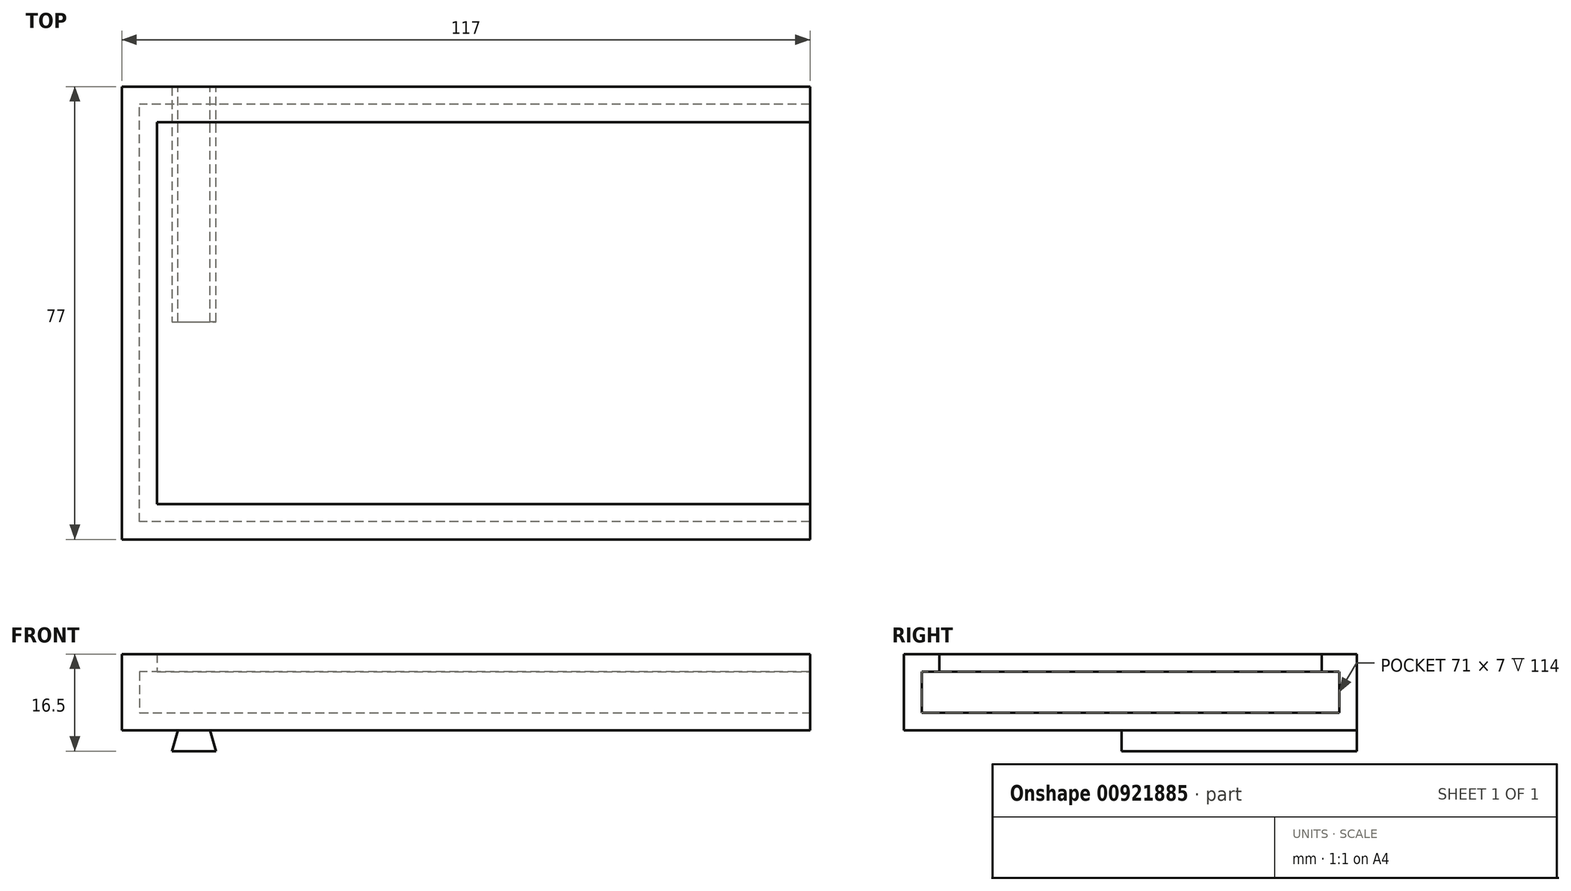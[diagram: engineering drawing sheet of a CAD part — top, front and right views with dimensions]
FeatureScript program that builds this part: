
annotation { "Feature Type Name" : "Feature", "Feature Type Description" : "" }
export const myFeature = defineFeature(function(context is Context, id is Id, definition is map)
    precondition{}
    {
        {
            var Q0;
            Q0=qCreatedBy(makeId("Top.planeOp"),FACE);
            var sketch = newSketch(context, id + "F0", { "sketchPlane" : qUnion([Q0])});
            skLineSegment(sketch, "E0.bottom", {"start": v(0, 0) * mm, "end": v(117, 0) * mm});
            skLineSegment(sketch, "E0.top", {"start": v(0, 77) * mm, "end": v(117, 77) * mm});
            skLineSegment(sketch, "E0.left", {"start": v(0, 0) * mm, "end": v(0, 77) * mm});
            skLineSegment(sketch, "E0.right", {"start": v(117, 0) * mm, "end": v(117, 77) * mm});
            skSolve(sketch);
        }
        {
            var Q0;
            Q0 = qSketchRegion(id + "F0", true);
            var Q1;
            Q1=makeQuery(id+"F0.imprint","IMPRINT",FACE,{"disambiguationData":[TD([[makeQuery(id+"F0.imprint","IMPRINT",EDGE,{"derivedFrom":sQuery(id+"F0.wireOp",EDGE,"E0.bottom")}),1.0]])]});
            extrude(context, id + "F1", {"entities" : qUnion([Q0, Q1]), "depth" : 3 * mm, "offsetDistance" : 25 * mm});
        }
        {
            var Q0;
            Q0=makeQuery(id+"F1.opExtrude","CAP_FACE",FACE,{"disambiguationData":[OSD([sQuery(id+"F0.wireOp",EDGE,"E0.bottom"),sQuery(id+"F0.wireOp",EDGE,"E0.top"),sQuery(id+"F0.wireOp",EDGE,"E0.left"),sQuery(id+"F0.wireOp",EDGE,"E0.right")])],"isStart":false});
            var sketch = newSketch(context, id + "F2", { "sketchPlane" : qUnion([Q0])});
            skLineSegment(sketch, "E1", {"start": v(117, 3) * mm, "end": v(3, 3) * mm});
            skLineSegment(sketch, "E2", {"start": v(3, 3) * mm, "end": v(3, 74) * mm});
            skLineSegment(sketch, "E3", {"start": v(3, 74) * mm, "end": v(117, 74) * mm});
            skSolve(sketch);
        }
        {
            var Q0;
            Q0 = qSketchRegion(id + "F2", true);
            var Q1;
            {var subQ2=sQuery(id+"F2.wireOp",EDGE,"E1");Q1=makeQuery(id+"F2.imprint","IMPRINT",FACE,{"disambiguationData":[TD([[makeQuery(id+"F2.imprint","IMPRINT",EDGE,{"derivedFrom":subQ2}),1.0]])]});}
            extrude(context, id + "F3", {"entities" : qUnion([Q0, Q1]), "operationType" : NewBodyOperationType.ADD, "depth" : 10 * mm, "offsetDistance" : 25 * mm});
        }
        {
            var Q0;
            Q0=makeQuery(id+"F3.opExtrude","SWEPT_FACE",FACE,{"disambiguationData":[OSD([sQuery(id+"F2.wireOp",EDGE,"E2")])]});
            var sketch = newSketch(context, id + "F4", { "sketchPlane" : qUnion([Q0])});
            skLineSegment(sketch, "E4", {"start": v(3, 10) * mm, "end": v(74, 10) * mm});
            skSolve(sketch);
        }
        {
            var Q0;
            Q0 = qSketchRegion(id + "F4", true);
            var Q1;
            {var subQ0=sQuery(id+"F4.wireOp",EDGE,"E4");Q1=makeQuery(id+"F4.imprint","IMPRINT",FACE,{"disambiguationData":[TD([[makeQuery(id+"F4.imprint","IMPRINT",EDGE,{"derivedFrom":subQ0}),1.0]])]});}
            extrude(context, id + "F5", {"entities" : qUnion([Q0, Q1]), "operationType" : NewBodyOperationType.ADD, "depth" : 3 * mm, "offsetDistance" : 25 * mm});
        }
        {
            var Q0;
            Q0=makeQuery(id+"F3.opExtrude","SWEPT_FACE",FACE,{"disambiguationData":[OSD([sQuery(id+"F2.wireOp",EDGE,"E1")])]});
            var sketch = newSketch(context, id + "F6", { "sketchPlane" : qUnion([Q0])});
            skLineSegment(sketch, "E5", {"start": v(-6, 10) * mm, "end": v(-117, 10) * mm});
            skSolve(sketch);
        }
        {
            var Q0;
            Q0 = qSketchRegion(id + "F6", true);
            var Q1;
            {var subQ0=sQuery(id+"F6.wireOp",EDGE,"E5");Q1=makeQuery(id+"F6.imprint","IMPRINT",FACE,{"disambiguationData":[TD([[makeQuery(id+"F6.imprint","IMPRINT",EDGE,{"derivedFrom":subQ0}),-1.0]])]});}
            extrude(context, id + "F7", {"entities" : qUnion([Q0, Q1]), "operationType" : NewBodyOperationType.ADD, "depth" : 3 * mm, "offsetDistance" : 25 * mm});
        }
        {
            var Q0;
            Q0=makeQuery(id+"F3.opExtrude","SWEPT_FACE",FACE,{"disambiguationData":[OSD([sQuery(id+"F2.wireOp",EDGE,"E3")])]});
            var sketch = newSketch(context, id + "F8", { "sketchPlane" : qUnion([Q0])});
            skLineSegment(sketch, "E6", {"start": v(6, 10) * mm, "end": v(117, 10) * mm});
            skSolve(sketch);
        }
        {
            var Q0;
            Q0 = qSketchRegion(id + "F8", true);
            var Q1;
            {var subQ0=sQuery(id+"F8.wireOp",EDGE,"E6");Q1=makeQuery(id+"F8.imprint","IMPRINT",FACE,{"disambiguationData":[TD([[makeQuery(id+"F8.imprint","IMPRINT",EDGE,{"derivedFrom":subQ0}),1.0]])]});}
            extrude(context, id + "F9", {"entities" : qUnion([Q0, Q1]), "operationType" : NewBodyOperationType.ADD, "depth" : 3 * mm, "offsetDistance" : 25 * mm});
        }
        {
            var Q0;
            Q0=makeQuery(id+"F1.opExtrude","CAP_FACE",FACE,{"disambiguationData":[OSD([sQuery(id+"F0.wireOp",EDGE,"E0.bottom"),sQuery(id+"F0.wireOp",EDGE,"E0.top"),sQuery(id+"F0.wireOp",EDGE,"E0.left"),sQuery(id+"F0.wireOp",EDGE,"E0.right")])],"isStart":true});
            var sketch = newSketch(context, id + "F10", { "sketchPlane" : qUnion([Q0])});
            skLineSegment(sketch, "E7", {"start": v(8.5, -77) * mm, "end": v(8.5, -37) * mm});
            skLineSegment(sketch, "E8", {"start": v(8.5, -37) * mm, "end": v(16, -37) * mm});
            skLineSegment(sketch, "E9", {"start": v(16, -37) * mm, "end": v(16, -77) * mm});
            skSolve(sketch);
        }
        {
            var Q0;
            Q0 = qSketchRegion(id + "F10", true);
            var Q1;
            {var subQ0=sQuery(id+"F10.wireOp",EDGE,"E7");Q1=makeQuery(id+"F10.imprint","IMPRINT",FACE,{"disambiguationData":[TD([[makeQuery(id+"F10.imprint","IMPRINT",EDGE,{"derivedFrom":subQ0}),-1.0]])]});}
            extrude(context, id + "F11", {"entities" : qUnion([Q0, Q1]), "operationType" : NewBodyOperationType.ADD, "depth" : 3.5 * mm, "offsetDistance" : 25 * mm});
        }
        {
            var Q0;
            {var subQ0=sQuery(id+"F0.wireOp",EDGE,"E0.top");Q0=makeQuery(id+"F11.boolean.opBoolean","MERGE",FACE,{"derivedFrom":[makeQuery(id+"F3.boolean.opBoolean","MERGE",FACE,{"derivedFrom":[makeQuery(id+"F1.opExtrude","SWEPT_FACE",FACE,{"disambiguationData":[OSD([subQ0])]}),makeQuery(id+"F3.opExtrude","SWEPT_FACE",FACE,{"disambiguationData":[OSD([subQ0])]})]}),makeQuery(id+"F11.opExtrude","SWEPT_FACE",FACE,{"disambiguationData":[OSD([subQ0])]})]});}
            var sketch = newSketch(context, id + "F12", { "sketchPlane" : qUnion([Q0])});
            skLineSegment(sketch, "E10", {"start": v(-16, -3.5) * mm, "end": v(-15, 0) * mm});
            skLineSegment(sketch, "E11", {"start": v(-15, 0) * mm, "end": v(-16, 0) * mm});
            skLineSegment(sketch, "E12", {"start": v(-8.5, -3.5) * mm, "end": v(-9.5, 0) * mm});
            skLineSegment(sketch, "E13", {"start": v(-9.5, 0) * mm, "end": v(-8.5, 0) * mm});
            skSolve(sketch);
        }
        {
            var Q0;
            Q0=makeQuery(id+"F12.imprint","IMPRINT",FACE,{"disambiguationData":[TD([[makeQuery(id+"F12.imprint","IMPRINT",EDGE,{"derivedFrom":sQuery(id+"F12.wireOp",EDGE,"E10")}),1.0]])]});
            extrude(context, id + "F13", {"entities" : qUnion([Q0]), "operationType" : NewBodyOperationType.REMOVE, "oppositeDirection" : true, "depth" : 40 * mm, "offsetDistance" : 25 * mm});
        }
        {
            var Q0;
            Q0=makeQuery(id+"F12.imprint","IMPRINT",FACE,{"disambiguationData":[TD([[makeQuery(id+"F12.imprint","IMPRINT",EDGE,{"derivedFrom":sQuery(id+"F12.wireOp",EDGE,"E12")}),-1.0]])]});
            extrude(context, id + "F14", {"entities" : qUnion([Q0]), "operationType" : NewBodyOperationType.REMOVE, "oppositeDirection" : true, "depth" : 40 * mm, "offsetDistance" : 25 * mm});
        }
    });
